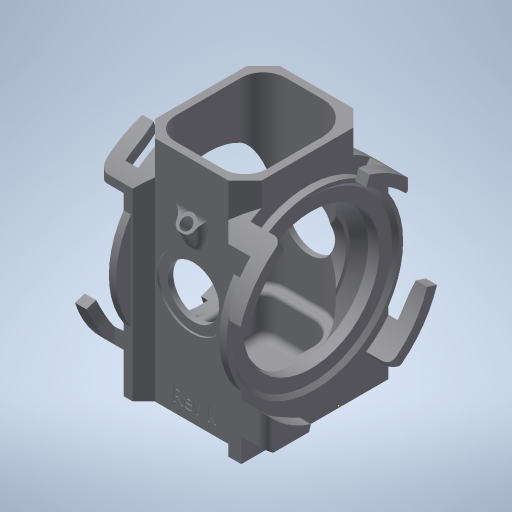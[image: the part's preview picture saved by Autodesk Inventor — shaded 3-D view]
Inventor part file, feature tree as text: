
AUTODESK INVENTOR PART (.ipt)
format: ipt  version: 2023.2 (Build 272271030, 271C)  size: 1,684,480 bytes
history: native  units: mm
features: sketch x36, extrude x18, hole x17, chamfer x17, projected_geometry x16, plane x6, fillet x5, thicken_offset x5, split x5, other x4, mirror x2, move_body x2, surface_op x2, direct_edit x2, pattern_circular x1, boolean_combine x1, emboss x1
ambient origin geometry x8: Origin, YZ Plane, XZ Plane, XY Plane, X Axis, Y Axis, Z Axis, Center Point
bodies: Solid1 (feature_tree), Solid2 (feature_tree), Solid3 (feature_tree)
feature tree (140):
  extrude  "Extrusion1"  Depth=40.0mm
  hole  "Hole5"  [1 undecoded]
  chamfer  "Chamfer2"  Distance=2.0mm Angle=45.0deg
  hole  "Hole6"  [1 undecoded]
  extrude  "Extrusion2"  Depth=10.0mm TaperAngle=0.0deg
  hole  "Hole14"  [1 undecoded]
  mirror  "Mirror2"
  extrude  "Extrusion6"  Depth=3.0mm
  hole  "Hole1"  [1 undecoded]
  hole  "Hole8"  [1 undecoded]
  hole  "Hole2"  [1 undecoded]
  hole  "Hole3"  [1 undecoded]
  hole  "Hole4"  [1 undecoded]
  mirror  "Mirror1"
  extrude  "Extrusion5"  Depth=61.0mm
  chamfer  "Chamfer1"  Distance=7.0mm
  chamfer  "Chamfer3"  Distance=2.0mm Angle=45.0deg
  extrude  "Extrusion3"  Depth=44.0mm
  chamfer  "Chamfer4"  Distance=1.5mm
  hole  "Hole11"  [1 undecoded]
  plane  "Work Plane1"
  extrude  "Extrusion8"  Depth=2.0mm
  chamfer  "Chamfer5"  Distance=1.5mm
  extrude  "Extrusion7"  [1 undecoded]
  chamfer  "Chamfer6"  Distance=2.0mm
  hole  "Hole12"  [1 undecoded]
  hole  "Hole13"  [1 undecoded]
  hole  "Hole7"  [1 undecoded]
  hole  "Hole9"  [1 undecoded]
  hole  "Hole10"  [1 undecoded]
  extrude  "Extrusion4"  Depth=2.0mm TaperAngle=0.0deg
  extrude  "Extrusion9"  Depth=2.0mm TaperAngle=0.0deg
  fillet  "Fillet1"  Radius=1.745329mm
  extrude  "Extrusion10"  TaperAngle=90.0deg  [1 undecoded]
  hole  "Hole15"  [1 undecoded]
  extrude  "Extrusion11"  Depth=2.0mm
  extrude  "Extrusion12"  Depth=2.0mm
  extrude  "Extrusion13"  Depth=2.0mm
  fillet  "Fillet2"  Radius=2.0mm
  chamfer  "Chamfer7"  Distance=0.2mm
  chamfer  "Chamfer8"  Distance=2.0mm
  chamfer  "Chamfer9"  Distance=2.0mm
  chamfer  "Chamfer10"  Angle=90.0deg  [1 undecoded]
  chamfer  "Chamfer11"  Angle=90.0deg  [1 undecoded]
  plane  "Work Plane2"
  extrude  "Extrusion14"  Depth=2.0mm
  pattern_circular  "Circular Pattern1"  [2 undecoded]
  thicken_offset  "Thicken1"
  plane  "Work Plane4"
  other  "Work Axis1"
  split  "Split1"
  move_body  "Move Body1"
  move_body  "Move Body2"
  surface_op  "Sculpt1"
  boolean_combine  "Combine1"
  extrude  "Extrusion15"  Depth=10.0mm TaperAngle=0.0deg
  extrude  "Extrusion16"  Depth=2.0mm
  extrude  "Extrusion17"  Depth=40.0mm TaperAngle=360.0deg
  fillet  "Fillet4"  Radius=23.5mm
  fillet  "Fillet3"  Radius=7.0mm
  extrude  "Extrusion18"  Depth=2.0mm
  plane  "Work Plane3"
  fillet  "Fillet5"  Radius=11.0mm
  hole  "Hole16"  [1 undecoded]
  hole  "Hole17"  [1 undecoded]
  emboss  "Emboss1"
  chamfer  "Chamfer12"  Distance=10.5mm
  chamfer  "Chamfer13"  Distance=1.0mm
  chamfer  "Chamfer14"  Distance=2.0mm
  chamfer  "Chamfer16"  Distance=2.0mm
  plane  "Work Plane5"
  split  "Split2"
  sketch  "Sketch37"  dims[d287=39.2mm d288=6.0mm d289=4.0mm d290=2.0mm d291=90.0deg d292=1.0mm d293=0.0mm d294=2.0mm d295=0.0mm d296=14.5mm d297=44.0mm d298=6.0mm d299=4.0mm d300=2.0mm d301=90.0deg d302=1.0mm d303=0.0mm d304=48.0mm d305=56.0mm d306=10.0mm d307=0.0mm d308=25.2mm d309=2.5mm d310=0.0mm d311=4.0mm d312=0.0mm d314=1.745329mm d318=90.0deg d320=2.0mm d321=0.2mm d322=2.0mm d323=15.184364mm d324=0.2mm d325=2.0mm d326=15.184364mm d327=0.2mm d328=2.0mm d329=15.184364mm d330=0.2mm d331=2.0mm d332=15.184364mm d333=1.0mm d334=2.0mm d335=15.184364mm d336=90.0deg d337=90.0deg d338=3.490659mm d339=25.2mm d340=10.0mm d341=0.0mm d343=20.0mm d344=40.0mm d345=360.0deg d347=23.5mm d348=7.0mm d349=0.0mm d354=2.5mm d355=11.0mm d356=0.0mm d357=0.8mm d358=1.2mm d359=10.5mm d360=0.0mm d361=1.0mm d362=2.0mm d364=2.0mm d365=2.0mm d366=1.8mm d367=10.5mm d368=0.0mm d369=4.0mm d371=45.0deg d373=45.0deg d374=4.0mm d375=1.5mm d376=7.5mm d377=5.0mm d378=0.0mm d379=1.0mm d380=3.15mm d381=6.0mm d382=5.1mm d383=1.0mm d384=90.0deg d385=20.0mm d386=0.0mm d387=2.0mm d390=30.0mm d391=26.0mm d392=4.1mm d393=6.0mm d394=4.4mm d395=4.775mm d396=90.0deg d397=8.0mm d398=0.0mm d399=0.8mm d400=2.0mm d401=24.0mm d402=3.5mm d403=0.0mm d404=180.0deg d405=-28.0mm d406=0.0mm d407=0.0mm d408=0.2mm d409=0.0mm d410=1.0mm d411=2.0mm d412=9.948377mm d413=1.0mm d414=2.0mm d415=12.740904mm d416=1.0mm d417=2.0mm d418=9.773844mm d422=2.0mm d423=2.0mm d424=15.0deg d426=4.0mm d427=4.0mm d428=4.0mm d429=4.0mm d430=3.0mm d431=3.25mm d432=4.0mm d433=4.0mm d434=4.0mm d435=4.0mm d436=2.0mm d437=2.0mm d438=90.0deg d439=2.0mm d440=2.0mm d441=90.0deg d57=14.3117mm d58=0.75mm d286=0.375mm d313=20.594885mm d315=0.75mm d316=0.375mm d350=0.872665mm d351=0.872665mm d352=0.5mm d353=0.872665mm d370=0.5mm d372=0.5mm]
  thicken_offset  "Thicken3"
  split  "Split3"
  thicken_offset  "Thicken4"
  direct_edit  "Direct Edit2"
  direct_edit  "Direct Edit3"
  plane  "Work Plane6"
  split  "Split4"
  thicken_offset  "Thicken5"
  split  "Split5"
  thicken_offset  "Thicken6"
  chamfer  "Chamfer17"  Distance=2.0mm
  chamfer  "Chamfer18"  Distance=1.8mm
  sketch  "Sketch1"  dims[d0=29.0mm d1=40.0mm]
  sketch  "Sketch2"  dims[d2=55.0mm d3=0.0mm]
  sketch  "Sketch3"  dims[d4=24.0mm d5=6.0mm d6=6.5mm d7=3.4mm d8=14.3117mm d9=61.0mm d10=0.0mm]
  sketch  "Sketch4"  dims[d11=23.5mm]
  sketch  "Sketch5"  dims[d12=20.0mm d13=6.0mm d14=4.0mm d15=2.0mm d16=90.0deg d17=3.0mm d18=0.0mm]
  sketch  "Sketch6"  dims[d19=18.9mm d20=6.0mm d21=4.0mm d22=2.0mm d23=90.0deg d24=0.5mm d25=0.0mm]
  sketch  "Sketch7"  dims[d26=14.0mm d27=6.0mm d28=4.0mm d29=2.0mm d30=90.0deg d31=5.0mm d32=0.0mm]
  sketch  "Sketch8"  dims[d33=3.0mm d34=2.0mm d35=45.0deg]
  sketch  "Sketch10"  dims[d37=37.0mm d38=6.0mm d39=4.0mm d40=2.0mm d41=90.0deg d42=4.5mm d43=0.0mm]
  sketch  "Sketch11"  dims[d44=30.0mm d45=6.0mm d46=4.0mm d47=2.0mm d48=90.0deg d49=19.5mm d50=0.0mm d51=2.5mm d52=2.0mm d53=45.0deg]
  sketch  "Sketch12"  dims[d54=40.0mm d55=10.0mm d56=0.0mm]
  sketch  "Sketch13"  dims[d59=33.0mm d60=5.0mm d61=4.0mm d62=2.0mm d63=90.0deg d64=1.5mm d65=0.0mm]
  projected_geometry  "Projected Loop1"
  sketch  "Sketch14"  dims[d66=26.0mm d67=6.0mm d68=4.0mm d69=2.0mm d70=90.0deg d71=44.0mm d72=20.594885mm]
  projected_geometry  "Projected Loop2"
  sketch  "Sketch15"  dims[d73=23.5mm d74=0.0mm d75=3.0mm]
  sketch  "Sketch16"  dims[d76=2.0mm d77=45.0deg d78=14.0mm]
  sketch  "Sketch17"  dims[d79=6.0mm d80=4.0mm d81=2.0mm d82=90.0deg d83=14.0mm d84=0.0mm]
  sketch  "Sketch18"  dims[d85=18.9mm]
  sketch  "Sketch19"  dims[d86=6.0mm d87=4.0mm d88=2.0mm d89=90.0deg d90=0.5mm d91=0.0mm]
  sketch  "Sketch20"  dims[d92=23.5mm d93=0.0mm d94=0.0mm]
  projected_geometry  "Projected Loop3"
  sketch  "Sketch21"  dims[d96=25.0mm d97=30.0mm]
  projected_geometry  "Projected Loop4"
  sketch  "Sketch22"  dims[d98=6.0mm d99=61.0mm]
  sketch  "Sketch23"  dims[d100=0.0mm]
  sketch  "Sketch24"  dims[d101=29.0mm]
  sketch  "Sketch25"  dims[d102=52.0mm d103=7.0mm d104=0.0mm d105=2.0mm d106=2.0mm d107=45.0deg]
  sketch  "Sketch26"  dims[d110=1.0mm d134=44.0mm]
  projected_geometry  "Projected Loop7"
  sketch  "Sketch27"  dims[d135=4.5mm d136=6.0mm d137=8.0mm d138=4.6mm d139=90.0deg d140=1.5mm d141=0.0mm d249=1.5mm d252=1.5mm]
  projected_geometry  "Projected Loop8"
  sketch  "Sketch28"  dims[d253=4.5mm d254=0.0mm d255=10.0mm d256=0.0mm]
  projected_geometry  "Projected Loop9"
  projected_geometry  "Projected Loop10"
  projected_geometry  "Projected Loop11"
  projected_geometry  "Projected Loop12"
  sketch  "Sketch29"  dims[d257=4.5mm d258=2.0mm d259=45.0deg d260=6.0mm d261=2.0mm d262=6.981317mm]
  projected_geometry  "Projected Loop13"
  sketch  "Sketch30"  dims[d264=4.0mm d265=8.0mm d266=77.0mm d267=50.0mm d268=90.0deg d269=8.5mm d270=20.594885mm]
  projected_geometry  "Projected Loop14"
  sketch  "Sketch31"  dims[d271=4.0mm]
  projected_geometry  "Projected Loop15"
  sketch  "Sketch32"  dims[d272=5.0mm]
  projected_geometry  "Projected Loop16"
  sketch  "Sketch33"  dims[d273=4.0mm d274=10.0mm d275=4.0mm d276=2.0mm d277=90.0deg d278=20.0mm d279=0.0mm]
  projected_geometry  "Projected Loop17"
  sketch  "Sketch34"  dims[d280=9.0mm]
  projected_geometry  "Projected Loop18"
  sketch  "Sketch35"  dims[d281=7.0mm d282=1.5mm d283=0.0mm]
  sketch  "Sketch36"  dims[d284=1.0mm d285=-1.5mm]
  surface_op  "Surface1"
  other  "Srf1"
  other  "Size2"
  other  "Size3"
note: 23 required parameter values undecoded (feature->parameter linkage not recoverable at this tier; creation-order binding heuristic only, values carry confidence <= 0.55)
